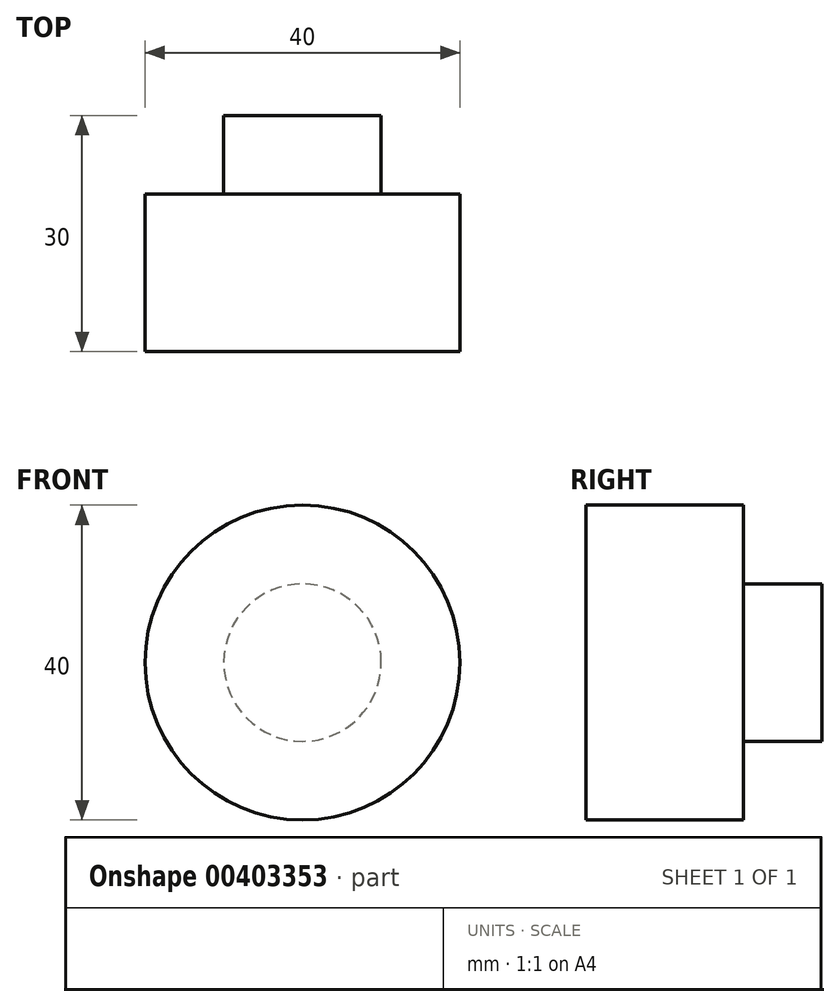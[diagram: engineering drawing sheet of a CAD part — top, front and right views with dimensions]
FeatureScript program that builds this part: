
annotation { "Feature Type Name" : "Feature", "Feature Type Description" : "" }
export const myFeature = defineFeature(function(context is Context, id is Id, definition is map)
    precondition{}
    {
        {
            var Q0;
            Q0=qCreatedBy(makeId("Right.planeOp"),FACE);
            var sketch = newSketch(context, id + "F0", { "sketchPlane" : qUnion([Q0])});
            skLineSegment(sketch, "E0.bottom", {"start": v(0, 0) * mm, "end": v(30, 0) * mm});
            skLineSegment(sketch, "E0.top", {"start": v(20, 10) * mm, "end": v(30, 10) * mm});
            skLineSegment(sketch, "E0.left", {"start": v(0, 0) * mm, "end": v(0, 10) * mm});
            skLineSegment(sketch, "E0.right", {"start": v(30, 0) * mm, "end": v(30, 10) * mm});
            skLineSegment(sketch, "E1", {"start": v(29.05, 0) * mm, "end": v(0, 0) * mm, "construction": true});
            skPoint(sketch, "E2.orphan", {"position": v(36.8, 0) * mm});
            skLineSegment(sketch, "E3.bottom", {"start": v(0, 0) * mm, "end": v(20, 0) * mm});
            skLineSegment(sketch, "E3.top", {"start": v(0, 20) * mm, "end": v(20, 20) * mm});
            skLineSegment(sketch, "E3.left", {"start": v(0, 0) * mm, "end": v(0, 20) * mm});
            skLineSegment(sketch, "E3.right", {"start": v(20, 10) * mm, "end": v(20, 20) * mm});
            skSolve(sketch);
        }
        {
            var Q0;
            Q0 = qSketchRegion(id + "F0", true);
            var Q1;
            Q1=sQuery(id+"F0.wireOp",EDGE,"E1");
            revolve(context, id + "F1", {"entities" : qUnion([Q0]), "axis" : qUnion([Q1]), "revolveType" : RevolveType.FULL});
        }
    });
